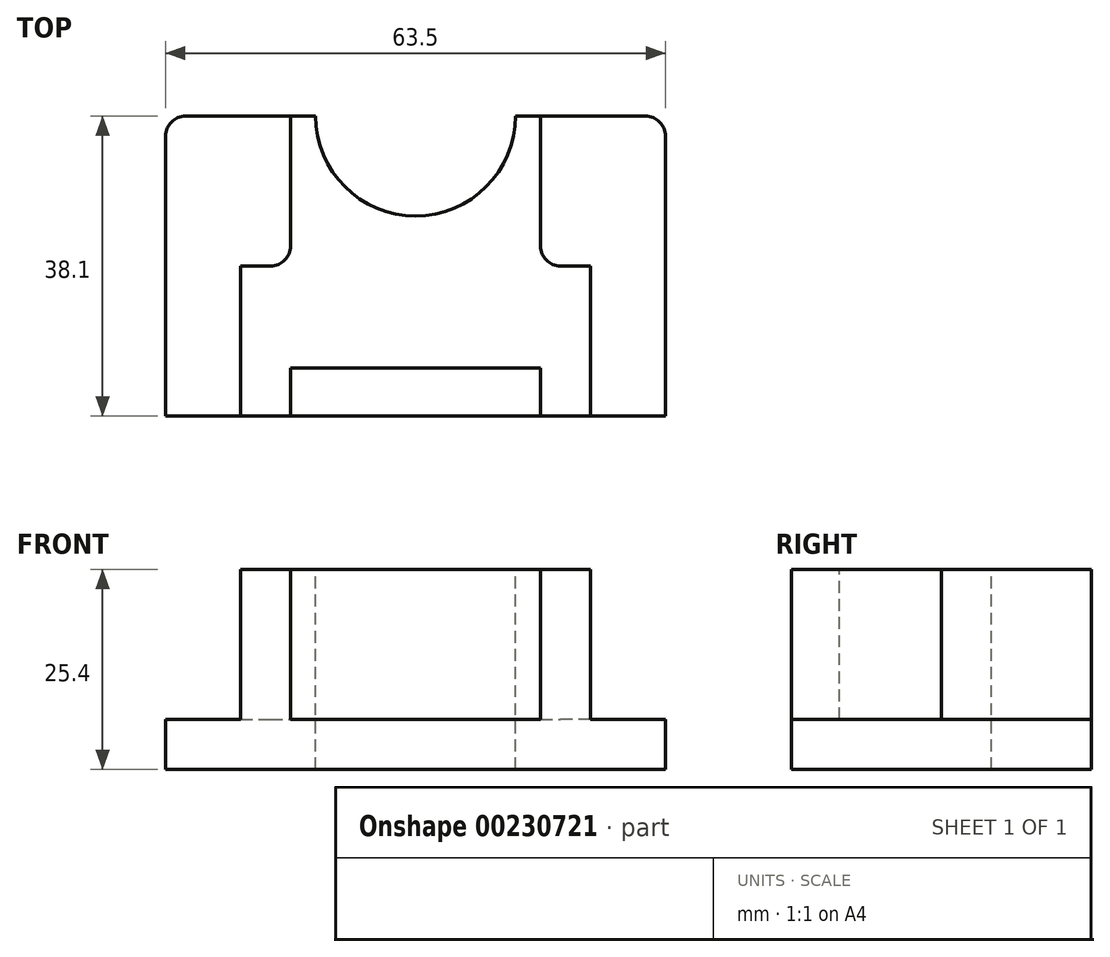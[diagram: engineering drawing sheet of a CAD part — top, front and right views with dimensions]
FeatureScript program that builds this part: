
annotation { "Feature Type Name" : "Feature", "Feature Type Description" : "" }
export const myFeature = defineFeature(function(context is Context, id is Id, definition is map)
    precondition{}
    {
        {
            var Q0;
            Q0=qCreatedBy(makeId("Top.planeOp"),FACE);
            var sketch = newSketch(context, id + "F0", { "sketchPlane" : qUnion([Q0])});
            skLineSegment(sketch, "E0.bottom", {"start": v(-31.75, 19.05) * mm, "end": v(31.75, 19.05) * mm});
            skLineSegment(sketch, "E0.top", {"start": v(-31.75, -19.05) * mm, "end": v(31.75, -19.05) * mm});
            skLineSegment(sketch, "E0.left", {"start": v(-31.75, 19.05) * mm, "end": v(-31.75, -19.05) * mm});
            skLineSegment(sketch, "E0.right", {"start": v(31.75, 19.05) * mm, "end": v(31.75, -19.05) * mm});
            skPoint(sketch, "E0.middle", {"position": v(0, 0) * mm});
            skSolve(sketch);
        }
        {
            var Q0;
            Q0=makeQuery(id+"F0.imprint","IMPRINT",FACE,{"disambiguationData":[TD([[makeQuery(id+"F0.imprint","IMPRINT",EDGE,{"derivedFrom":sQuery(id+"F0.wireOp",EDGE,"E0.bottom")}),-1.0]])]});
            extrude(context, id + "F1", {"entities" : qUnion([Q0]), "depth" : 6.35 * mm});
        }
        {
            var Q0;
            Q0=makeQuery(id+"F1.opExtrude","CAP_FACE",FACE,{"disambiguationData":[OSD([sQuery(id+"F0.wireOp",EDGE,"E0.bottom"),sQuery(id+"F0.wireOp",EDGE,"E0.top"),sQuery(id+"F0.wireOp",EDGE,"E0.left"),sQuery(id+"F0.wireOp",EDGE,"E0.right")])],"isStart":false});
            var sketch = newSketch(context, id + "F2", { "sketchPlane" : qUnion([Q0])});
            skLineSegment(sketch, "E1.bottom", {"start": v(22.23, 19.05) * mm, "end": v(-22.23, 19.05) * mm});
            skLineSegment(sketch, "E1.top", {"start": v(22.23, -19.05) * mm, "end": v(-22.23, -19.05) * mm});
            skLineSegment(sketch, "E1.left", {"start": v(22.23, 19.05) * mm, "end": v(22.23, -19.05) * mm});
            skLineSegment(sketch, "E1.right", {"start": v(-22.23, 19.05) * mm, "end": v(-22.23, -19.05) * mm});
            skPoint(sketch, "E1.middle", {"position": v(0, 0) * mm});
            skSolve(sketch);
        }
        {
            var Q0;
            Q0=makeQuery(id+"F2.imprint","IMPRINT",FACE,{"disambiguationData":[TD([[makeQuery(id+"F2.imprint","IMPRINT",EDGE,{"derivedFrom":sQuery(id+"F2.wireOp",EDGE,"E1.bottom")}),-1.0]])]});
            extrude(context, id + "F3", {"entities" : qUnion([Q0]), "operationType" : NewBodyOperationType.ADD, "depth" : 19.05 * mm});
        }
        {
            var Q0;
            Q0=makeQuery(id+"F3.opExtrude","CAP_FACE",FACE,{"disambiguationData":[OSD([sQuery(id+"F2.wireOp",EDGE,"E1.bottom"),sQuery(id+"F2.wireOp",EDGE,"E1.top"),sQuery(id+"F2.wireOp",EDGE,"E1.left"),sQuery(id+"F2.wireOp",EDGE,"E1.right")])],"isStart":false});
            var sketch = newSketch(context, id + "F4", { "sketchPlane" : qUnion([Q0])});
            skLineSegment(sketch, "E2.bottom", {"start": v(-15.88, -12.97) * mm, "end": v(15.88, -12.97) * mm});
            skLineSegment(sketch, "E2.top", {"start": v(-15.88, -25.13) * mm, "end": v(15.88, -25.13) * mm});
            skLineSegment(sketch, "E2.left", {"start": v(-15.88, -12.97) * mm, "end": v(-15.88, -25.13) * mm});
            skLineSegment(sketch, "E2.right", {"start": v(15.88, -12.97) * mm, "end": v(15.88, -25.13) * mm});
            skPoint(sketch, "E2.middle", {"position": v(0, -19.05) * mm});
            skSolve(sketch);
        }
        {
            var Q0;
            Q0 = qSketchRegion(id + "F4", true);
            extrude(context, id + "F5", {"entities" : qUnion([Q0]), "operationType" : NewBodyOperationType.REMOVE, "oppositeDirection" : true, "depth" : 19.05 * mm});
        }
        {
            var Q0;
            Q0=makeQuery(id+"F3.opExtrude","CAP_FACE",FACE,{"disambiguationData":[OSD([sQuery(id+"F2.wireOp",EDGE,"E1.bottom"),sQuery(id+"F2.wireOp",EDGE,"E1.top"),sQuery(id+"F2.wireOp",EDGE,"E1.left"),sQuery(id+"F2.wireOp",EDGE,"E1.right")])],"isStart":false});
            var sketch = newSketch(context, id + "F6", { "sketchPlane" : qUnion([Q0])});
            skCircle(sketch, "E3", {"center": v(0, 19.05) * mm, "radius": 12.7 * mm});
            skSolve(sketch);
        }
        {
            var Q0;
            {var subQ0=sQuery(id+"F6.wireOp",EDGE,"E3");var subQ1=makeQuery(id+"F3.opExtrude","CAP_EDGE",EDGE,{"disambiguationData":[OSD([sQuery(id+"F2.wireOp",EDGE,"E1.bottom")])],"isStart":false});var subQ2=makeQuery(id+"F6.imprint","INTERSECT",VERTEX,{"disambiguationData":[OD(0.0)],"derivedFrom":[subQ1,subQ0]});Q0=makeQuery(id+"F6.imprint","IMPRINT",FACE,{"disambiguationData":[TD([[makeQuery(id+"F6.imprint","IMPRINT",EDGE,{"disambiguationData":[TD([[subQ2,1.0]])],"derivedFrom":subQ0}),1.0]])]});}
            var Q1;
            {var subQ0=sQuery(id+"F6.wireOp",EDGE,"E3");var subQ1=makeQuery(id+"F3.opExtrude","CAP_EDGE",EDGE,{"disambiguationData":[OSD([sQuery(id+"F2.wireOp",EDGE,"E1.bottom")])],"isStart":false});var subQ2=makeQuery(id+"F6.imprint","INTERSECT",VERTEX,{"disambiguationData":[OD(0.0)],"derivedFrom":[subQ1,subQ0]});Q1=makeQuery(id+"F6.imprint","IMPRINT",FACE,{"disambiguationData":[TD([[makeQuery(id+"F6.imprint","IMPRINT",EDGE,{"disambiguationData":[TD([[subQ2,-1.0]])],"derivedFrom":subQ0}),1.0]])]});}
            extrude(context, id + "F7", {"entities" : qUnion([Q0, Q1]), "operationType" : NewBodyOperationType.REMOVE, "endBound" : BoundingType.THROUGH_ALL, "oppositeDirection" : true, "depth" : 25.4 * mm});
        }
        {
            var Q0;
            Q0=makeQuery(id+"F3.opExtrude","CAP_FACE",FACE,{"disambiguationData":[OSD([sQuery(id+"F2.wireOp",EDGE,"E1.bottom"),sQuery(id+"F2.wireOp",EDGE,"E1.top"),sQuery(id+"F2.wireOp",EDGE,"E1.left"),sQuery(id+"F2.wireOp",EDGE,"E1.right")])],"isStart":false});
            var sketch = newSketch(context, id + "F8", { "sketchPlane" : qUnion([Q0])});
            skSolve(sketch);
        }
        {
            var Q0;
            {var subQ2=sQuery(id+"F2.wireOp",EDGE,"E1.left");Q0=makeQuery(id+"F8.imprint","IMPRINT",FACE,{"disambiguationData":[TD([[makeQuery(id+"F8.imprint","IMPRINT",EDGE,{"derivedFrom":makeQuery(id+"F3.opExtrude","CAP_EDGE",EDGE,{"disambiguationData":[OSD([subQ2])],"isStart":false})}),-1.0]])]});}
            var sketch = newSketch(context, id + "F9", { "sketchPlane" : qUnion([Q0])});
            skLineSegment(sketch, "E4.bottom", {"start": v(-22.23, 19.05) * mm, "end": v(-15.88, 19.05) * mm});
            skLineSegment(sketch, "E4.top", {"start": v(-22.23, 0) * mm, "end": v(-15.88, 0) * mm});
            skLineSegment(sketch, "E4.left", {"start": v(-22.23, 19.05) * mm, "end": v(-22.23, 0) * mm});
            skLineSegment(sketch, "E4.right", {"start": v(-15.88, 19.05) * mm, "end": v(-15.88, 0) * mm});
            skSolve(sketch);
        }
        {
            var Q0;
            Q0 = qSketchRegion(id + "F9", true);
            extrude(context, id + "F10", {"entities" : qUnion([Q0]), "operationType" : NewBodyOperationType.REMOVE, "oppositeDirection" : true, "depth" : 19.05 * mm});
        }
        {
            var Q0;
            {var subQ2=sQuery(id+"F2.wireOp",EDGE,"E1.left");Q0=makeQuery(id+"F8.imprint","IMPRINT",FACE,{"disambiguationData":[TD([[makeQuery(id+"F8.imprint","IMPRINT",EDGE,{"derivedFrom":makeQuery(id+"F3.opExtrude","CAP_EDGE",EDGE,{"disambiguationData":[OSD([subQ2])],"isStart":false})}),-1.0]])]});}
            var sketch = newSketch(context, id + "F11", { "sketchPlane" : qUnion([Q0])});
            skLineSegment(sketch, "E5.bottom", {"start": v(22.22, 19.05) * mm, "end": v(15.87, 19.05) * mm});
            skLineSegment(sketch, "E5.top", {"start": v(22.23, 0) * mm, "end": v(15.88, 0) * mm});
            skLineSegment(sketch, "E5.left", {"start": v(22.22, 19.05) * mm, "end": v(22.23, 0) * mm});
            skLineSegment(sketch, "E5.right", {"start": v(15.87, 19.05) * mm, "end": v(15.88, 0) * mm});
            skSolve(sketch);
        }
        {
            var Q0;
            Q0=makeQuery(id+"F11.imprint","IMPRINT",FACE,{"disambiguationData":[TD([[makeQuery(id+"F11.imprint","IMPRINT",EDGE,{"derivedFrom":sQuery(id+"F11.wireOp",EDGE,"E5.bottom")}),-1.0]])]});
            extrude(context, id + "F12", {"entities" : qUnion([Q0]), "operationType" : NewBodyOperationType.REMOVE, "oppositeDirection" : true, "depth" : 19.05 * mm});
        }
        {
            var Q0;
            Q0=makeQuery(id+"F12.boolean.opBoolean","COPY",EDGE,{"derivedFrom":makeQuery(id+"F12.opExtrude","SWEPT_EDGE",EDGE,{"disambiguationData":[OSD([sQuery(id+"F11.wireOp",EDGE,"E5.top"),sQuery(id+"F11.wireOp",EDGE,"E5.right")])]})});
            fillet(context, id + "F13", {"entities" : qUnion([Q0]), "radius" : 2.54 * mm, "tangentPropagation" : true, "allowEdgeOverflow" : false});
        }
        {
            var Q0;
            Q0=makeQuery(id+"F10.boolean.opBoolean","COPY",EDGE,{"derivedFrom":makeQuery(id+"F10.opExtrude","SWEPT_EDGE",EDGE,{"disambiguationData":[OSD([sQuery(id+"F9.wireOp",EDGE,"E4.top"),sQuery(id+"F9.wireOp",EDGE,"E4.right")])]})});
            fillet(context, id + "F14", {"entities" : qUnion([Q0]), "radius" : 2.54 * mm, "tangentPropagation" : true, "allowEdgeOverflow" : false});
        }
        {
            var Q0;
            Q0=makeQuery(id+"F1.opExtrude","SWEPT_EDGE",EDGE,{"disambiguationData":[OSD([sQuery(id+"F0.wireOp",EDGE,"E0.bottom"),sQuery(id+"F0.wireOp",EDGE,"E0.left")])]});
            fillet(context, id + "F15", {"entities" : qUnion([Q0]), "radius" : 2.54 * mm, "tangentPropagation" : true, "allowEdgeOverflow" : false});
        }
        {
            var Q0;
            Q0=makeQuery(id+"F1.opExtrude","SWEPT_EDGE",EDGE,{"disambiguationData":[OSD([sQuery(id+"F0.wireOp",EDGE,"E0.bottom"),sQuery(id+"F0.wireOp",EDGE,"E0.right")])]});
            fillet(context, id + "F16", {"entities" : qUnion([Q0]), "radius" : 2.54 * mm, "tangentPropagation" : true, "allowEdgeOverflow" : false});
        }
    });
